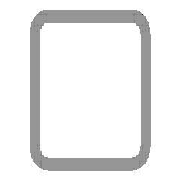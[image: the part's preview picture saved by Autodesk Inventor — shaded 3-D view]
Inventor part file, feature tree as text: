
AUTODESK INVENTOR PART (.ipt)
format: ipt  version: 2025.3 (Build 293356030, 356C)  size: 134,144 bytes
history: native  units: mm (DEFAULTED — no unit token found)
features: other x4, sketch x1, plane x1
ambient origin geometry x8: Origin, YZ Plane, XZ Plane, XY Plane, X Axis, Y Axis, Z Axis, Center Point
bodies: Solid1 (feature_tree), Body (feature_tree)
feature tree (6):
  parser-record x1  (decoder bookkeeping rows leaked as tree rows — omitted from the tree; the rows remain in map.json)
  other  "Driven Length"
  other  "Start Plane"
  other  "End Plane"
  sketch  "Sketch3"  dims[d3=170.0mm d4=0.0mm d7=4.0mm d9=40.0mm d11=40.0mm d12=2.0mm d13=-0.0mm d14=170.0mm d15=20.0mm d16=20.0mm d17=90.0deg d18=170.0mm]
  plane  "Work Plane3"
